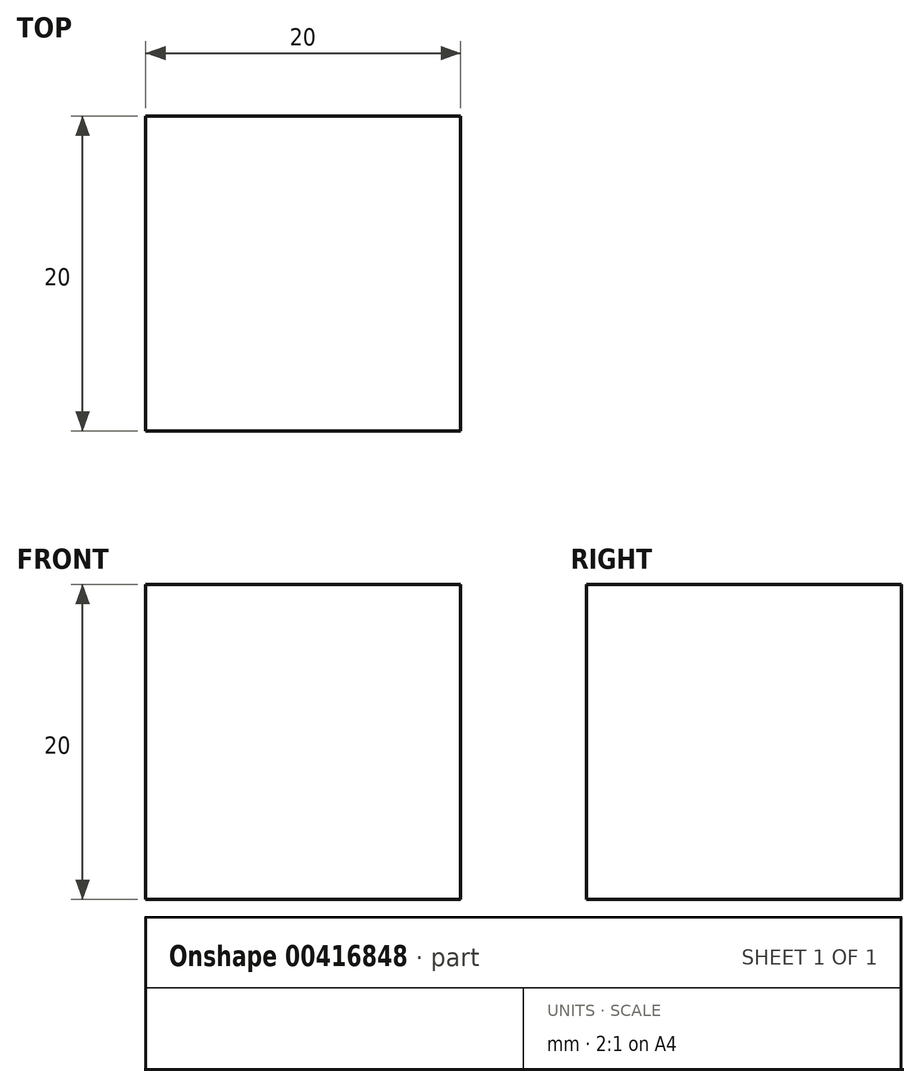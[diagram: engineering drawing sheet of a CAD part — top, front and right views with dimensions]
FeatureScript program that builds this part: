
annotation { "Feature Type Name" : "Feature", "Feature Type Description" : "" }
export const myFeature = defineFeature(function(context is Context, id is Id, definition is map)
    precondition{}
    {
        {
            var Q0;
            Q0=qCreatedBy(makeId("Top.planeOp"),FACE);
            var sketch = newSketch(context, id + "F0", { "sketchPlane" : qUnion([Q0])});
            skLineSegment(sketch, "E0.bottom", {"start": v(31.01, 36.52) * mm, "end": v(51.01, 36.52) * mm});
            skLineSegment(sketch, "E0.top", {"start": v(31.01, 56.52) * mm, "end": v(51.01, 56.52) * mm});
            skLineSegment(sketch, "E0.left", {"start": v(31.01, 36.52) * mm, "end": v(31.01, 56.52) * mm});
            skLineSegment(sketch, "E0.right", {"start": v(51.01, 36.52) * mm, "end": v(51.01, 56.52) * mm});
            skSolve(sketch);
        }
        {
            var Q0;
            Q0=makeQuery(id+"F0.imprint","IMPRINT",FACE,{"disambiguationData":[TD([[makeQuery(id+"F0.imprint","IMPRINT",EDGE,{"derivedFrom":sQuery(id+"F0.wireOp",EDGE,"E0.bottom")}),1.0]])]});
            extrude(context, id + "F1", {"entities" : qUnion([Q0]), "depth" : 20 * mm});
        }
    });
